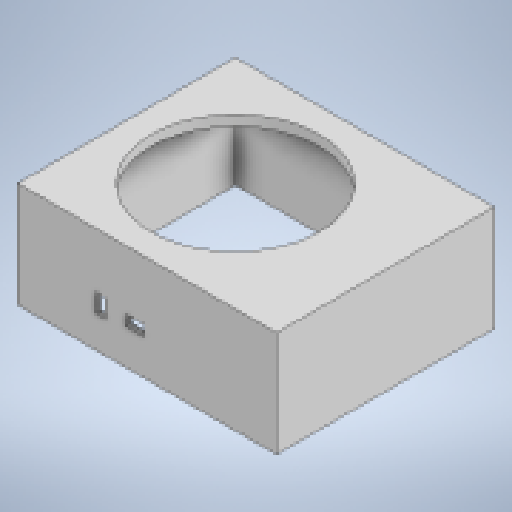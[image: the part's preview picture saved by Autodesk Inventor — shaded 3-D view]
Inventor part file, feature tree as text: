
AUTODESK INVENTOR PART (.ipt)
format: ipt  version: 2024.2 (Build 282272000, 272)  size: 165,888 bytes
history: native  units: in
note: dims shown in document units (in); Inventor stores cm internally (conversion verified against a paired STEP export)
features: extrude x3, sketch x3
ambient origin geometry x8: Origin, YZ Plane, XZ Plane, XY Plane, X Axis, Y Axis, Z Axis, Center Point
bodies: Solid1 (feature_tree)
feature tree (6):
  extrude  "Extrusion1"  Depth=4.1732in
  extrude  "Extrusion3"  Depth=0.0984in
  extrude  "Extrusion4"  Depth=1.8228in TaperAngle=0.0deg
  sketch  "Sketch1"  dims[d0=4.9606in d1=4.1732in]
  sketch  "Sketch3"  dims[d2=2.0197in d3=0.0in d8=0.0984in]
  sketch  "Sketch4"  dims[d9=0.0984in d10=1.8228in d11=0.0in d12=3.2283in d13=2.876in d14=1.8228in d15=0.0in d16=0.1969in d17=0.3465in d18=0.6152in d19=1.4941in d20=0.3465in d21=0.1969in d22=0.3937in d23=0.3937in d24=0.0in]
